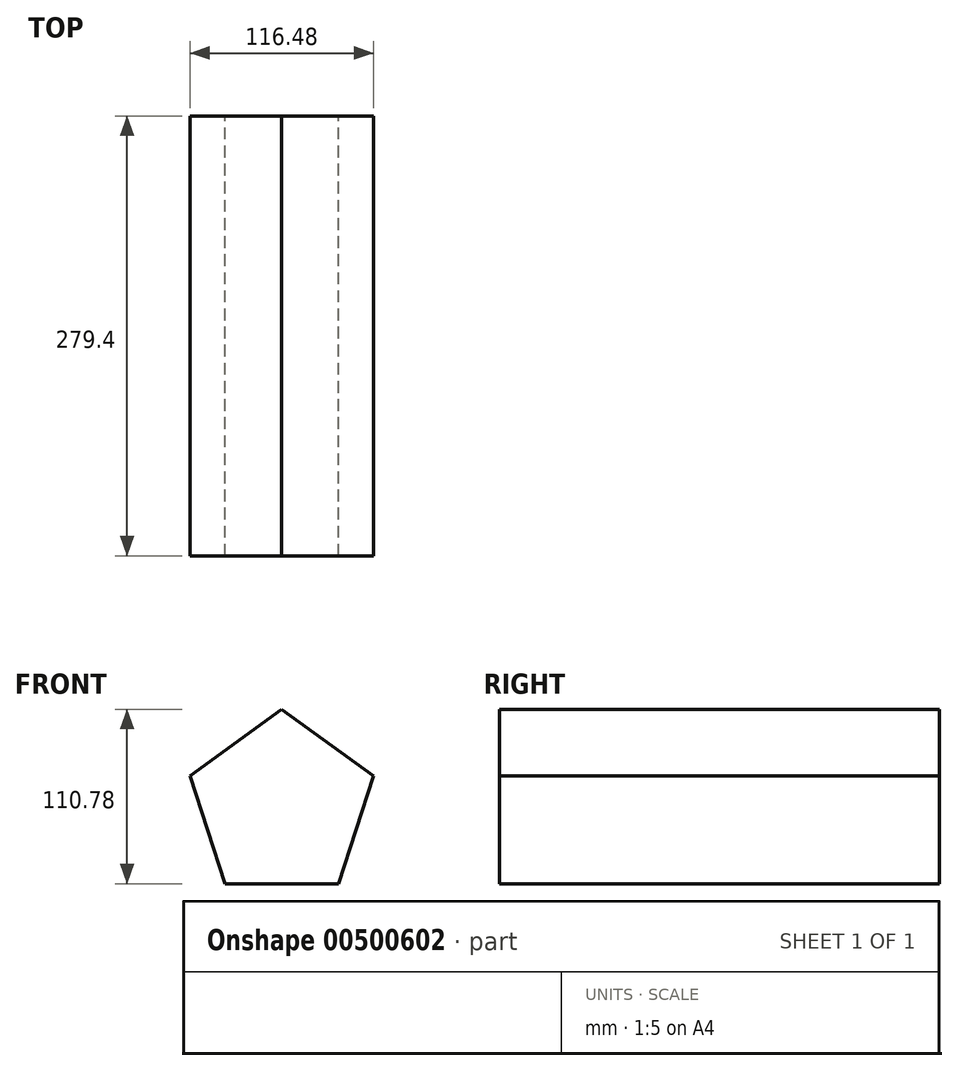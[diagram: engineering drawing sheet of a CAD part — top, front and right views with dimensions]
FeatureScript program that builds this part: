
annotation { "Feature Type Name" : "Feature", "Feature Type Description" : "" }
export const myFeature = defineFeature(function(context is Context, id is Id, definition is map)
    precondition{}
    {
        {
            var Q0;
            Q0=qCreatedBy(makeId("Front.planeOp"),FACE);
            var sketch = newSketch(context, id + "F0", { "sketchPlane" : qUnion([Q0])});
            skCircle(sketch, "E0.cCircle", {"center": v(0, 2.74) * mm, "radius": 61.24 * mm, "construction": true});
            skLineSegment(sketch, "E0.0", {"start": v(0, 63.98) * mm, "end": v(58.24, 21.67) * mm});
            skLineSegment(sketch, "E0.1", {"start": v(58.24, 21.67) * mm, "end": v(36, -46.8) * mm});
            skLineSegment(sketch, "E0.2", {"start": v(36, -46.8) * mm, "end": v(-36, -46.8) * mm});
            skLineSegment(sketch, "E0.3", {"start": v(-36, -46.8) * mm, "end": v(-58.24, 21.67) * mm});
            skLineSegment(sketch, "E0.4", {"start": v(-58.24, 21.67) * mm, "end": v(0, 63.98) * mm});
            skSolve(sketch);
        }
        {
            var Q0;
            Q0 = qSketchRegion(id + "F0", true);
            extrude(context, id + "F1", {"entities" : qUnion([Q0]), "depth" : 279.4 * mm});
        }
    });
